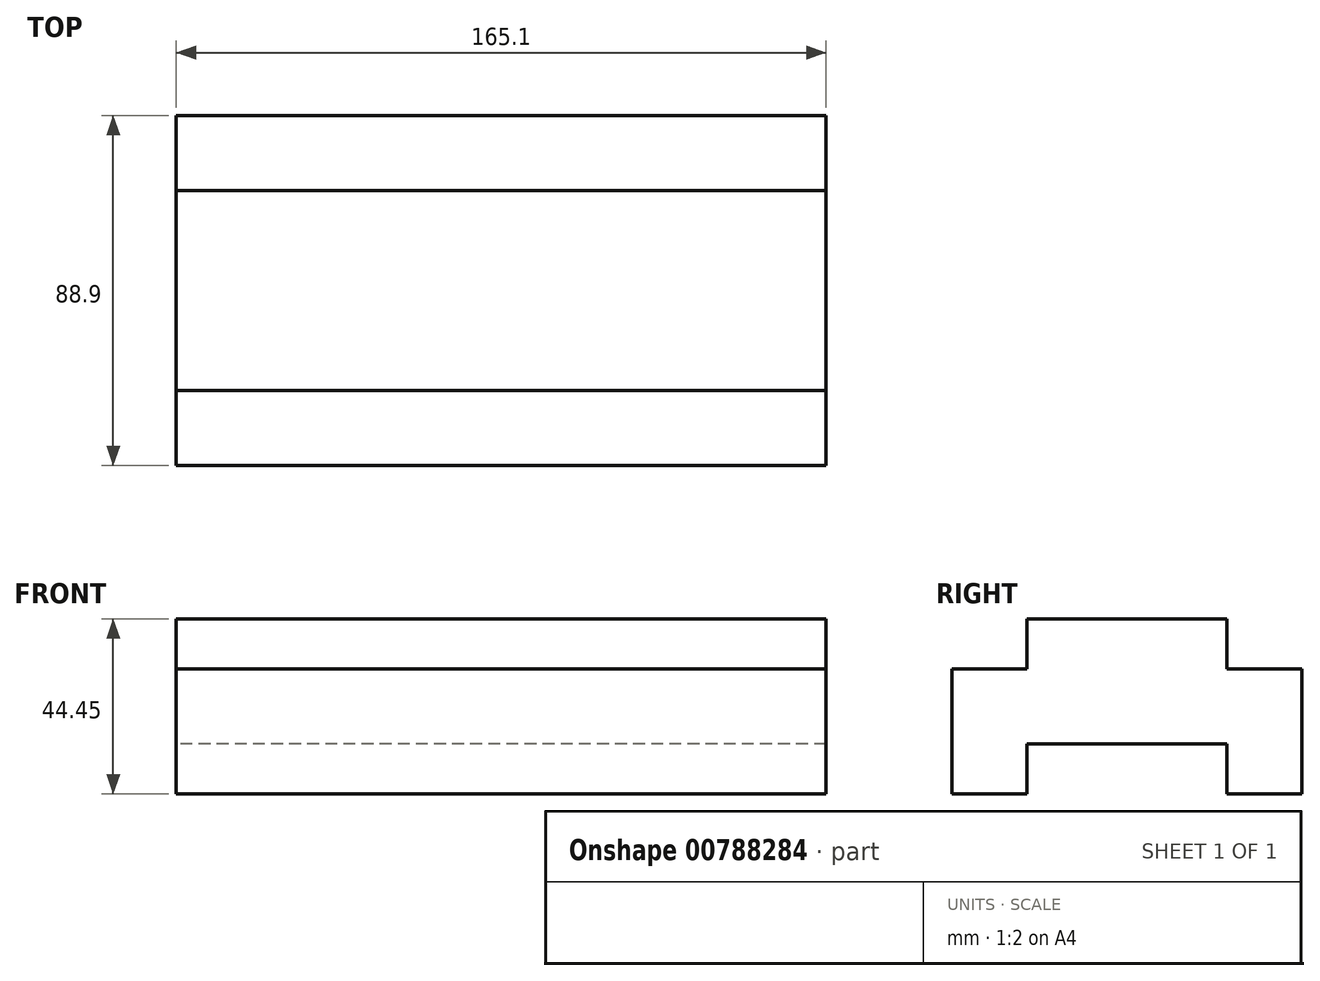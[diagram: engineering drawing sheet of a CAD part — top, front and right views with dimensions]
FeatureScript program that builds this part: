
annotation { "Feature Type Name" : "Feature", "Feature Type Description" : "" }
export const myFeature = defineFeature(function(context is Context, id is Id, definition is map)
    precondition{}
    {
        {
            var Q0;
            Q0=qCreatedBy(makeId("Right.planeOp"),FACE);
            var sketch = newSketch(context, id + "F0", { "sketchPlane" : qUnion([Q0])});
            skLineSegment(sketch, "E0", {"start": v(0, 0) * mm, "end": v(19.05, 0) * mm});
            skLineSegment(sketch, "E1", {"start": v(19.05, 0) * mm, "end": v(19.05, 12.7) * mm});
            skLineSegment(sketch, "E2", {"start": v(19.05, 12.7) * mm, "end": v(69.85, 12.7) * mm});
            skLineSegment(sketch, "E3", {"start": v(69.85, 12.7) * mm, "end": v(69.85, 0) * mm});
            skLineSegment(sketch, "E4", {"start": v(69.85, 0) * mm, "end": v(88.9, 0) * mm});
            skLineSegment(sketch, "E5", {"start": v(88.9, 0) * mm, "end": v(88.9, 31.75) * mm});
            skLineSegment(sketch, "E6", {"start": v(88.9, 31.75) * mm, "end": v(69.85, 31.75) * mm});
            skLineSegment(sketch, "E7", {"start": v(69.85, 31.75) * mm, "end": v(69.85, 44.45) * mm});
            skLineSegment(sketch, "E8", {"start": v(69.85, 44.45) * mm, "end": v(19.05, 44.45) * mm});
            skLineSegment(sketch, "E9", {"start": v(19.05, 44.45) * mm, "end": v(19.05, 31.75) * mm});
            skLineSegment(sketch, "E10", {"start": v(19.05, 31.75) * mm, "end": v(0, 31.75) * mm});
            skLineSegment(sketch, "E11", {"start": v(0, 31.75) * mm, "end": v(0, 0) * mm});
            skSolve(sketch);
        }
        {
            var Q0;
            Q0 = qSketchRegion(id + "F0", true);
            extrude(context, id + "F1", {"entities" : qUnion([Q0]), "depth" : 165.1 * mm, "offsetDistance" : 25.4 * mm});
        }
    });
